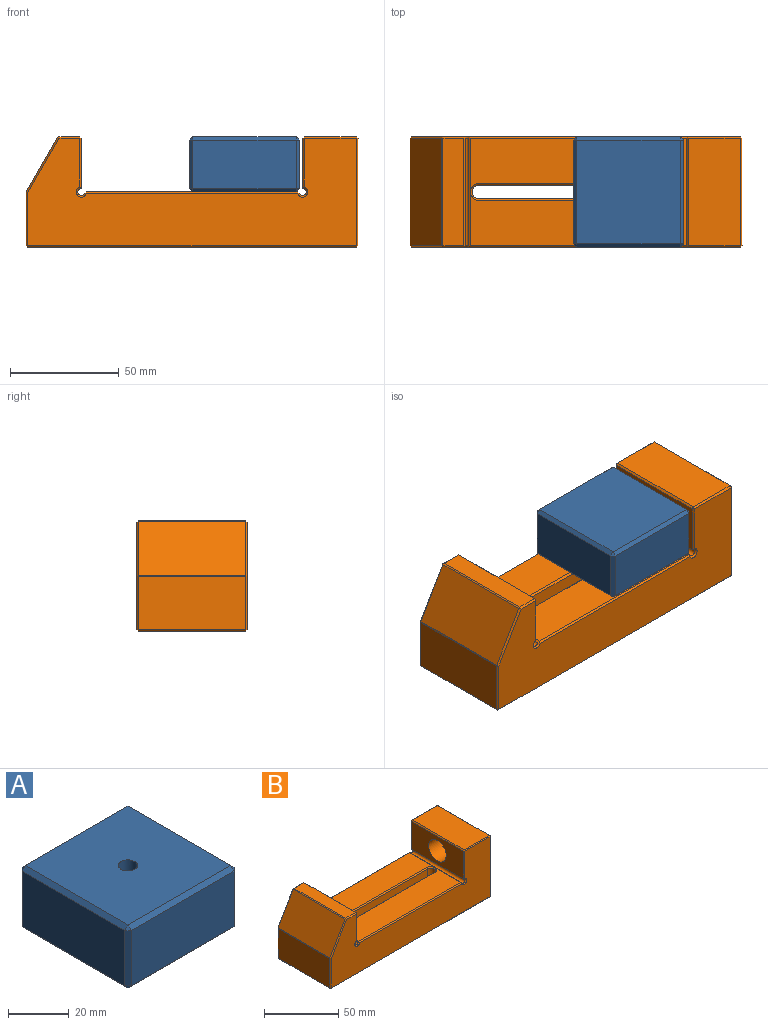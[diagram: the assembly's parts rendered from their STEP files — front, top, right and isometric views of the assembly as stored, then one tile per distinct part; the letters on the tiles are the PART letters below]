
ASSEMBLY  parts=2 mates=1
PART A: 29 faces, bbox 50.8x50.8x25.4 mm
  f0: plane 47.63x22.23mm, normal (1,0,0), area 931.8mm2, adj f6,f9,f12,f16,f17
  f1: plane 47.63x22.23mm, normal (0,1,0), area 1058.5mm2, adj f12,f13,f22,f23
  f2: plane 47.63x22.23mm, normal (-1,0,0), area 1058.5mm2, adj f14,f23,f24,f28
  f3: plane 47.63x22.23mm, normal (0,-1,0), area 1058.5mm2, adj f15,f16,f24,f25
  f4: plane 47.63x47.63mm, normal (0,0,1), area 2236.5mm2, adj f8,f9,f13,f14,f15
  f5: plane 47.63x47.63mm, normal (0,0,-1), area 2268.1mm2, adj f17,f22,f25,f28
  f6: cylinder r=6.35mm len=38.1mm, axis (1,0,0), area 1487.3mm2, adj f0,f7,f8
  f7: plane 12.7x12.7mm, normal (1,0,0), area 126.7mm2, adj f6
  f8: cylinder r=3.17mm len=7.2mm, axis (0,0,1), area 135mm2, adj f4,f6
  f9: plane 47.63x1.59mm, normal (0.71,0,0.71), area 106.9mm2, adj f0,f4,f10,f11
  f10: plane 1.59x1.59mm, normal (0.58,0.58,0.58), area 2.2mm2, adj f9,f12,f13
  f11: plane 1.59x1.59mm, normal (0.58,-0.58,0.58), area 2.2mm2, adj f9,f15,f16
  f12: plane 22.23x1.59mm, normal (0.71,0.71,0), area 49.9mm2, adj f0,f1,f10,f18
  f13: plane 47.63x1.59mm, normal (0,0.71,0.71), area 106.9mm2, adj f1,f4,f10,f19
  f14: plane 47.63x1.59mm, normal (-0.71,0,0.71), area 106.9mm2, adj f2,f4,f19,f20
  f15: plane 47.63x1.59mm, normal (0,-0.71,0.71), area 106.9mm2, adj f3,f4,f11,f20
  f16: plane 22.23x1.59mm, normal (0.71,-0.71,0), area 49.9mm2, adj f0,f3,f11,f21
  f17: plane 47.63x1.59mm, normal (0.71,0,-0.71), area 106.9mm2, adj f0,f5,f18,f21
  f18: plane 1.59x1.59mm, normal (0.58,0.58,-0.58), area 2.2mm2, adj f12,f17,f22
  f19: plane 1.59x1.59mm, normal (-0.58,0.58,0.58), area 2.2mm2, adj f13,f14,f23
  f20: plane 1.59x1.59mm, normal (-0.58,-0.58,0.58), area 2.2mm2, adj f14,f15,f24
  f21: plane 1.59x1.59mm, normal (0.58,-0.58,-0.58), area 2.2mm2, adj f16,f17,f25
  f22: plane 47.63x1.59mm, normal (0,0.71,-0.71), area 106.9mm2, adj f1,f5,f18,f26
  f23: plane 22.23x1.59mm, normal (-0.71,0.71,0), area 49.9mm2, adj f1,f2,f19,f26
  f24: plane 22.23x1.59mm, normal (-0.71,-0.71,0), area 49.9mm2, adj f2,f3,f20,f27
  f25: plane 47.63x1.59mm, normal (0,-0.71,-0.71), area 106.9mm2, adj f3,f5,f21,f27
  f26: plane 1.59x1.59mm, normal (-0.58,0.58,-0.58), area 2.2mm2, adj f22,f23,f28
  f27: plane 1.59x1.59mm, normal (-0.58,-0.58,-0.58), area 2.2mm2, adj f24,f25,f28
  f28: plane 47.63x1.59mm, normal (-0.71,0,-0.71), area 106.9mm2, adj f2,f5,f26,f27
PART B: 80 faces, bbox 152.5x50.9x50.9 mm
  f0: plane 150.81x49.21mm, normal (0,0,-1), area 5252.7mm2, adj f27,f35,f36,f37,f75,f76,f77,f78
  f1: plane 88.9x9.37mm, normal (0,-1,0), area 832.7mm2, adj f2,f4,f21,f22
  f2: cylinder r=3.17mm len=9.37mm, axis (0,0,1), area 93.4mm2, adj f1,f3,f21,f23
  f3: plane 88.9x9.37mm, normal (0,1,0), area 832.7mm2, adj f2,f4,f21,f25
  f4: cylinder r=3.17mm len=9.37mm, axis (0,0,1), area 93.4mm2, adj f1,f3,f21,f24
  f5: plane 49.21x49.21mm, normal (1,0,0), area 2203.7mm2, adj f36,f45,f46,f47,f79
  f6: plane 49.21x23.81mm, normal (0,0,1), area 1171.9mm2, adj f46,f55,f56,f57
  f7: plane 49.21x23.02mm, normal (-1,0,0), area 914.6mm2, adj f15,f56,f65,f66,f79
  f8: plane 97.11x49.21mm, normal (0,0,1), area 4023.9mm2, adj f22,f23,f24,f25,f63,f68,f71,f74
  f9: plane 49.21x23.02mm, normal (1,0,0), area 1132.8mm2, adj f16,f49,f54,f58
  f10: plane 49.21x9.48mm, normal (0,0,1), area 466.7mm2, adj f39,f44,f48,f49
  f11: plane 49.21x24.82mm, normal (-0.87,0,0.5), area 1410.4mm2, adj f29,f34,f38,f39
  f12: plane 49.21x24.39mm, normal (-1,0,0), area 1200.5mm2, adj f26,f27,f28,f29
  f13: plane 150.81x49.21mm, normal (0,-1,0), area 4605mm2, adj f28,f37,f38,f47,f48,f57,f58,f62
  f14: plane 150.81x49.21mm, normal (0,1,0), area 4605mm2, adj f26,f34,f35,f44,f45,f54,f55,f59
  f15: cylinder r=1.59mm len=49.21mm, axis (0,-1,0), area 341.6mm2, adj f7,f69,f70,f74
  f16: cylinder r=1.59mm len=49.21mm, axis (0,-1,0), area 341.6mm2, adj f9,f59,f62,f63
  f17: cylinder r=9.53mm len=19.05mm, axis (0,0,-1), area 432.3mm2, adj f18,f20,f21,f75
  f18: plane 88.9x14.45mm, normal (0,1,0), area 1284.3mm2, adj f17,f19,f21,f77
  f19: cylinder r=9.53mm len=19.05mm, axis (0,0,-1), area 432.3mm2, adj f18,f20,f21,f78
  f20: plane 88.9x14.45mm, normal (0,-1,0), area 1284.3mm2, adj f17,f19,f21,f76
  f21: plane 107.95x19.05mm, normal (0,0,-1), area 1382.4mm2, adj f1,f2,f3,f4,f17,f18,f19,f20
  f22: plane 88.9x0.79mm, normal (0,-0.71,0.71), area 99.8mm2, adj f1,f8,f23,f24
  f23: cone r=3.97mm half-angle=45deg, axis (0,0,1), area 12.6mm2, adj f2,f8,f22,f25
  f24: cone r=3.97mm half-angle=45deg, axis (0,0,1), area 12.6mm2, adj f4,f8,f22,f25
  f25: plane 88.9x0.79mm, normal (0,0.71,0.71), area 99.8mm2, adj f3,f8,f23,f24
  f26: plane 24.39x0.79mm, normal (-0.71,0.71,0), area 27.4mm2, adj f12,f14,f30,f31
  f27: plane 49.21x0.79mm, normal (-0.71,0,-0.71), area 55.2mm2, adj f0,f12,f31,f32
  f28: plane 24.39x0.79mm, normal (-0.71,-0.71,0), area 27.4mm2, adj f12,f13,f32,f33
  f29: plane 49.21x0.4mm, normal (-0.97,0,0.26), area 20.2mm2, adj f11,f12,f30,f33
  f30: plane 0.79x0.79mm, normal (-0.69,0.69,0.19), area 0.2mm2, adj f26,f29,f34
  f31: plane 0.79x0.79mm, normal (-0.58,0.58,-0.58), area 0.5mm2, adj f26,f27,f35
  f32: plane 0.79x0.79mm, normal (-0.58,-0.58,-0.58), area 0.5mm2, adj f27,f28,f37
  f33: plane 0.79x0.79mm, normal (-0.69,-0.69,0.19), area 0.2mm2, adj f28,f29,f38
  f34: plane 25.22x15.02mm, normal (-0.61,0.71,0.35), area 32.2mm2, adj f11,f14,f30,f40
  f35: plane 150.81x0.79mm, normal (0,0.71,-0.71), area 169.3mm2, adj f0,f14,f31,f41
  f36: plane 49.21x0.79mm, normal (0.71,0,-0.71), area 55.2mm2, adj f0,f5,f41,f42
  f37: plane 150.81x0.79mm, normal (0,-0.71,-0.71), area 169.3mm2, adj f0,f13,f32,f42
  f38: plane 25.22x15.02mm, normal (-0.61,-0.71,0.35), area 32.2mm2, adj f11,f13,f33,f43
  f39: plane 49.21x0.69mm, normal (-0.5,0,0.87), area 39.1mm2, adj f10,f11,f40,f43
  f40: plane 0.79x0.79mm, normal (-0.38,0.65,0.65), area 0.4mm2, adj f34,f39,f44
  f41: plane 0.79x0.79mm, normal (0.58,0.58,-0.58), area 0.5mm2, adj f35,f36,f45
  f42: plane 0.79x0.79mm, normal (0.58,-0.58,-0.58), area 0.5mm2, adj f36,f37,f47
  f43: plane 0.79x0.79mm, normal (-0.38,-0.65,0.65), area 0.4mm2, adj f38,f39,f48
  f44: plane 9.48x0.79mm, normal (0,0.71,0.71), area 10.6mm2, adj f10,f14,f40,f50
  f45: plane 49.21x0.79mm, normal (0.71,0.71,0), area 55.2mm2, adj f5,f14,f41,f51
  f46: plane 49.21x0.79mm, normal (0.71,0,0.71), area 55.2mm2, adj f5,f6,f51,f52
  f47: plane 49.21x0.79mm, normal (0.71,-0.71,0), area 55.2mm2, adj f5,f13,f42,f52
  f48: plane 9.48x0.79mm, normal (0,-0.71,0.71), area 10.6mm2, adj f10,f13,f43,f53
  f49: plane 49.21x0.79mm, normal (0.71,0,0.71), area 55.2mm2, adj f9,f10,f50,f53
  f50: plane 0.79x0.79mm, normal (0.58,0.58,0.58), area 0.5mm2, adj f44,f49,f54
  f51: plane 0.79x0.79mm, normal (0.58,0.58,0.58), area 0.5mm2, adj f45,f46,f55
  f52: plane 0.79x0.79mm, normal (0.58,-0.58,0.58), area 0.5mm2, adj f46,f47,f57
  f53: plane 0.79x0.79mm, normal (0.58,-0.58,0.58), area 0.5mm2, adj f48,f49,f58
  f54: plane 23.13x0.91mm, normal (0.71,0.71,0), area 25.4mm2, adj f9,f14,f50,f59
  f55: plane 23.81x0.79mm, normal (0,0.71,0.71), area 26.7mm2, adj f6,f14,f51,f60
  f56: plane 49.21x0.79mm, normal (-0.71,0,0.71), area 55.2mm2, adj f6,f7,f60,f61
  f57: plane 23.81x0.79mm, normal (0,-0.71,0.71), area 26.7mm2, adj f6,f13,f52,f61
  f58: plane 23.13x0.91mm, normal (0.71,-0.71,0), area 25.4mm2, adj f9,f13,f53,f62
  f59: cone r=2.38mm half-angle=45deg, axis (0,1,0), area 9.3mm2, adj f14,f16,f54,f64
  f60: plane 0.79x0.79mm, normal (-0.58,0.58,0.58), area 0.5mm2, adj f55,f56,f65
  f61: plane 0.79x0.79mm, normal (-0.58,-0.58,0.58), area 0.5mm2, adj f56,f57,f66
  f62: cone r=1.59mm half-angle=45deg, axis (0,-1,0), area 9.3mm2, adj f13,f16,f58,f67
  f63: plane 49.21x0.75mm, normal (-0.58,0,0.82), area 45.1mm2, adj f8,f16,f64,f67
  f64: plane 0.79x0.79mm, normal (-0.45,0.63,0.63), area 0.5mm2, adj f59,f63,f68
  f65: plane 23.13x0.91mm, normal (-0.71,0.71,0), area 25.4mm2, adj f7,f14,f60,f69
  f66: plane 23.13x0.91mm, normal (-0.71,-0.71,0), area 25.4mm2, adj f7,f13,f61,f70
  f67: plane 0.79x0.79mm, normal (-0.45,-0.63,0.63), area 0.5mm2, adj f62,f63,f71
  f68: plane 97.11x0.79mm, normal (0,0.71,0.71), area 109mm2, adj f8,f14,f64,f72
  f69: cone r=2.38mm half-angle=45deg, axis (0,1,0), area 9.3mm2, adj f14,f15,f65,f72
  f70: cone r=1.59mm half-angle=45deg, axis (0,-1,0), area 9.3mm2, adj f13,f15,f66,f73
  f71: plane 97.11x0.79mm, normal (0,-0.71,0.71), area 109mm2, adj f8,f13,f67,f73
  f72: plane 0.79x0.79mm, normal (0.45,0.63,0.63), area 0.5mm2, adj f68,f69,f74
  f73: plane 0.79x0.79mm, normal (0.45,-0.63,0.63), area 0.5mm2, adj f70,f71,f74
  f74: plane 49.21x0.75mm, normal (0.58,0,0.82), area 45.1mm2, adj f8,f15,f72,f73
  f75: cone r=10.32mm half-angle=45deg, axis (0,0,-1), area 35mm2, adj f0,f17,f76,f77
  f76: plane 88.9x0.79mm, normal (0,-0.71,-0.71), area 99.8mm2, adj f0,f20,f75,f78
  f77: plane 88.9x0.79mm, normal (0,0.71,-0.71), area 99.8mm2, adj f0,f18,f75,f78
  f78: cone r=10.32mm half-angle=45deg, axis (0,0,-1), area 35mm2, adj f0,f19,f76,f77
  f79: cylinder r=8.33mm len=25.4mm, axis (1,0,0), area 1330mm2, adj f5,f7
PLACE A rot(axis=(-1,0,0),180deg) t=(-51.96,-17.69,60.89)mm
PLACE B rot(axis=(0.56,0.32,0.77),0deg) t=(0.18,-17.69,10.09)mm fixed
MATE slider A.f6 <-> B.f79  axis (1,0,0) through (-26.56,-17.69,48.19)mm
